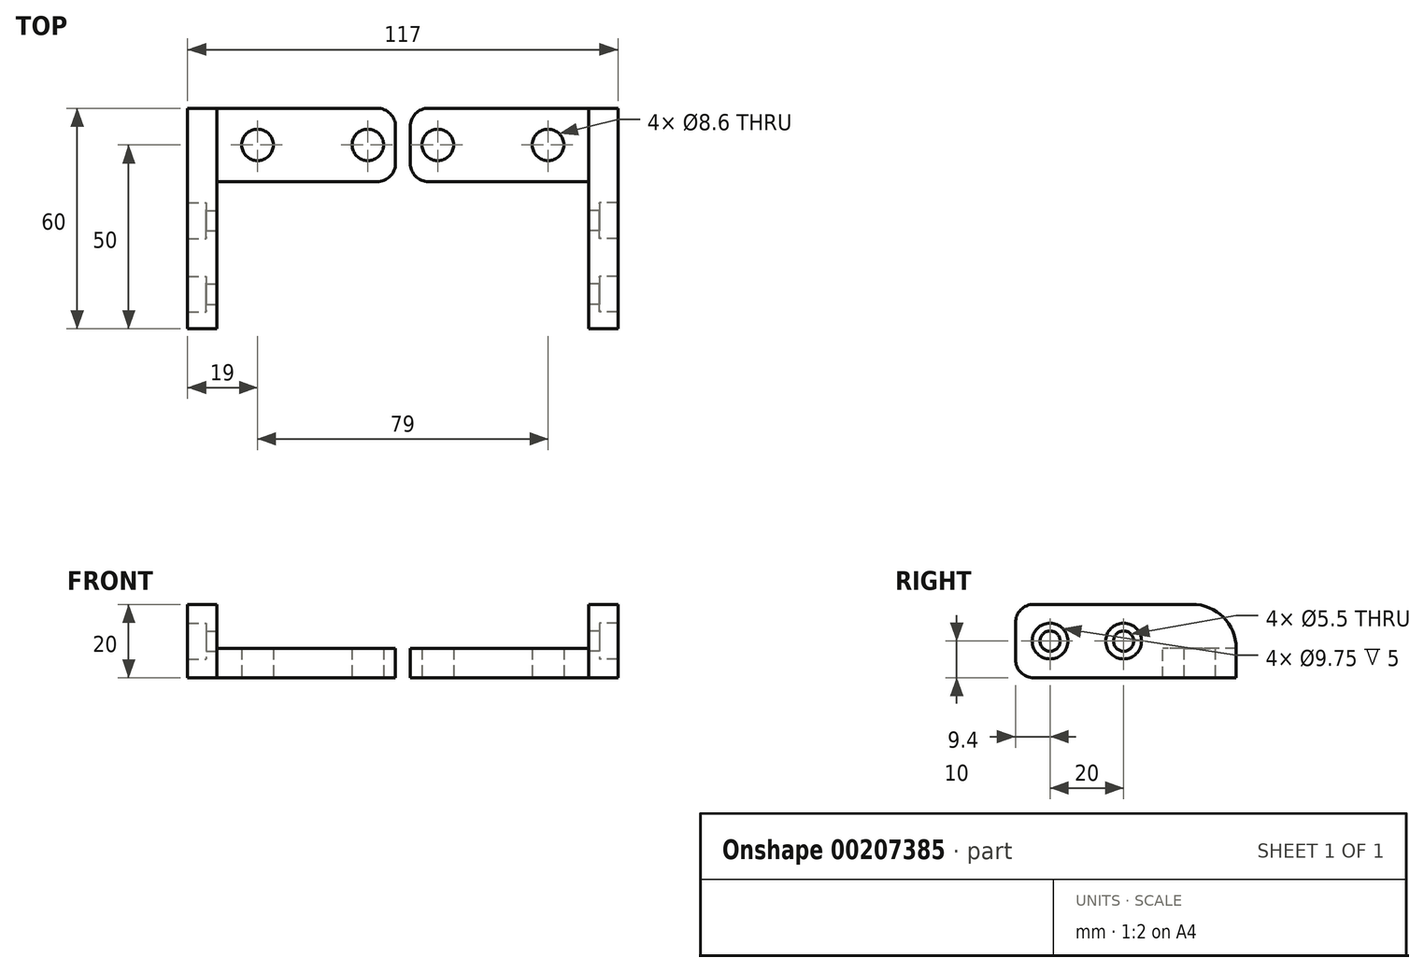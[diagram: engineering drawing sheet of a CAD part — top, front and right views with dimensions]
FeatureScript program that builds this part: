
annotation { "Feature Type Name" : "Feature", "Feature Type Description" : "" }
export const myFeature = defineFeature(function(context is Context, id is Id, definition is map)
    precondition{}
    {
        {
            var Q0;
            Q0=qCreatedBy(makeId("Top.planeOp"),FACE);
            var sketch = newSketch(context, id + "F0", { "sketchPlane" : qUnion([Q0])});
            skPoint(sketch, "E0", {"position": v(39.5, 50) * mm});
            skLineSegment(sketch, "E1.right", {"start": v(50.5, 60) * mm, "end": v(50.5, 40) * mm});
            skLineSegment(sketch, "E2", {"start": v(9.5, 29.4) * mm, "end": v(9.5, 9.4) * mm, "construction": true});
            skPoint(sketch, "E3", {"position": v(9.5, 19.4) * mm});
            skLineSegment(sketch, "E4.top", {"start": v(2, 0) * mm, "end": v(17, 0) * mm});
            skLineSegment(sketch, "E4.left", {"start": v(2, 60) * mm, "end": v(2, 0) * mm});
            skLineSegment(sketch, "E4.right", {"start": v(17, 40) * mm, "end": v(17, 0) * mm});
            skPoint(sketch, "E5", {"position": v(17, 19.4) * mm});
            skPoint(sketch, "E6", {"position": v(9.5, 0) * mm});
            skPoint(sketch, "E7", {"position": v(9.5, 29.4) * mm});
            skPoint(sketch, "E8", {"position": v(9.5, 9.4) * mm});
            skLineSegment(sketch, "E9", {"start": v(50.5, 40) * mm, "end": v(17, 40) * mm});
            skLineSegment(sketch, "E10", {"start": v(50.5, 60) * mm, "end": v(2, 60) * mm});
            skPoint(sketch, "E11", {"position": v(9.5, 50) * mm});
            skPoint(sketch, "E12", {"position": v(50.5, 50) * mm});
            skLineSegment(sketch, "E13", {"start": v(17, 40) * mm, "end": v(2, 40) * mm});
            skSolve(sketch);
        }
        {
            var Q0;
            Q0=makeQuery(id+"F0.imprint","IMPRINT",FACE,{"disambiguationData":[TD([[makeQuery(id+"F0.imprint","IMPRINT",EDGE,{"derivedFrom":sQuery(id+"F0.wireOp",EDGE,"E1.right")}),-1.0]])]});
            extrude(context, id + "F1", {"entities" : qUnion([Q0]), "oppositeDirection" : true, "depth" : 8 * mm, "offsetDistance" : 25 * mm});
        }
        {
            var Q0;
            Q0=sQuery(id+"F0.wireOp",VERTEX,"E11");
            var Q1;
            Q1=sQuery(id+"F0.wireOp",VERTEX,"E0");
            var Q2;
            Q2=makeQuery(id+"F1.opExtrude","SWEPT_BODY",BODY,{"disambiguationData":[OSD([sQuery(id+"F0.wireOp",EDGE,"E1.right"),sQuery(id+"F0.wireOp",EDGE,"E4.top"),sQuery(id+"F0.wireOp",EDGE,"E4.left"),sQuery(id+"F0.wireOp",EDGE,"E4.right"),sQuery(id+"F0.wireOp",EDGE,"E9"),sQuery(id+"F0.wireOp",EDGE,"E10")])]});
            hole(context, id + "F2", {"style" : HoleStyle.SIMPLE, "endStyle" : HoleEndStyle.THROUGH, "holeDiameter" : 8.6 * mm, "majorDiameter" : 5 * mm, "isTappedThrough" : true, "tappedDepth" : 12 * mm, "tapClearance" : 3, "locations" : qUnion([Q0, Q1]), "scope" : qUnion([Q2]), "startStyle" : HoleStartStyle.SKETCH});
        }
        {
            var Q0;
            Q0=makeQuery(id+"F1.opExtrude","SWEPT_FACE",FACE,{"disambiguationData":[OSD([sQuery(id+"F0.wireOp",EDGE,"E10")])]});
            var sketch = newSketch(context, id + "F3", { "sketchPlane" : qUnion([Q0])});
            skLineSegment(sketch, "E14.bottom", {"start": v(-50.5, -8) * mm, "end": v(-58.5, -8) * mm});
            skLineSegment(sketch, "E14.top", {"start": v(-50.5, 12) * mm, "end": v(-58.5, 12) * mm});
            skLineSegment(sketch, "E14.left", {"start": v(-50.5, -8) * mm, "end": v(-50.5, 12) * mm});
            skLineSegment(sketch, "E14.right", {"start": v(-58.5, -8) * mm, "end": v(-58.5, 12) * mm});
            skSolve(sketch);
        }
        {
            var Q0;
            {var subQ3=sQuery(id+"F3.wireOp",EDGE,"E14.bottom");Q0=makeQuery(id+"F3.imprint","IMPRINT",FACE,{"disambiguationData":[TD([[makeQuery(id+"F3.imprint","IMPRINT",EDGE,{"derivedFrom":subQ3}),-1.0]])]});}
            extrude(context, id + "F4", {"entities" : qUnion([Q0]), "operationType" : NewBodyOperationType.ADD, "oppositeDirection" : true, "depth" : 60 * mm, "offsetDistance" : 25 * mm});
        }
        {
            var Q0;
            Q0=makeQuery(id+"F4.opExtrude","SWEPT_FACE",FACE,{"disambiguationData":[OSD([sQuery(id+"F3.wireOp",EDGE,"E14.right")])]});
            var sketch = newSketch(context, id + "F5", { "sketchPlane" : qUnion([Q0])});
            skPoint(sketch, "E15", {"position": v(29.4, 2) * mm});
            skPoint(sketch, "E15.positionSnap0", {"position": v(60, 2) * mm});
            skPoint(sketch, "E16", {"position": v(9.4, 2) * mm});
            skPoint(sketch, "E17.0", {"position": v(50, 0) * mm});
            skSolve(sketch);
        }
        {
            var Q0;
            Q0=sQuery(id+"F5.wireOp",VERTEX,"E16");
            var Q1;
            Q1=sQuery(id+"F5.wireOp",VERTEX,"E15");
            var Q2;
            Q2=makeQuery(id+"F1.opExtrude","SWEPT_BODY",BODY,{"disambiguationData":[OSD([sQuery(id+"F0.wireOp",EDGE,"E1.right"),sQuery(id+"F0.wireOp",EDGE,"E4.top"),sQuery(id+"F0.wireOp",EDGE,"E4.left"),sQuery(id+"F0.wireOp",EDGE,"E4.right"),sQuery(id+"F0.wireOp",EDGE,"E9"),sQuery(id+"F0.wireOp",EDGE,"E10")])]});
            hole(context, id + "F6", {"style" : HoleStyle.C_BORE, "endStyle" : HoleEndStyle.BLIND, "standardTappedOrClearance" : lookupTablePath({ "fit" : "Normal", "standard" : "ISO", "size" : "M5", "type" : "Clearance" }), "standardBlindInLast" : lookupTablePath({ "fit" : "Normal", "standard" : "ISO", "engagement" : "75%", "pitch" : "0.8 mm", "size" : "M5", "type" : "Clearance & tapped" }), "holeDiameter" : 5.5 * mm, "cBoreDiameter" : 9.75 * mm, "cBoreDepth" : 5 * mm, "majorDiameter" : 5 * mm, "holeDepth" : 30 * mm, "isTappedThrough" : true, "tappedDepth" : 12 * mm, "tapClearance" : 3, "locations" : qUnion([Q0, Q1]), "scope" : qUnion([Q2]), "startStyle" : HoleStartStyle.SKETCH});
        }
        {
            var Q0;
            Q0=makeQuery(id+"F4.opExtrude","CAP_EDGE",EDGE,{"disambiguationData":[OSD([sQuery(id+"F3.wireOp",EDGE,"E14.top")])],"isStart":true});
            fillet(context, id + "F7", {"entities" : qUnion([Q0]), "radius" : 12 * mm, "tangentPropagation" : true, "allowEdgeOverflow" : false});
        }
        {
            var Q0;
            Q0=makeQuery(id+"F4.opExtrude","CAP_EDGE",EDGE,{"disambiguationData":[OSD([sQuery(id+"F3.wireOp",EDGE,"E14.top")])],"isStart":false});
            var Q1;
            Q1=makeQuery(id+"F4.opExtrude","CAP_EDGE",EDGE,{"disambiguationData":[OSD([sQuery(id+"F3.wireOp",EDGE,"E14.bottom")])],"isStart":false});
            var Q2;
            Q2=makeQuery(id+"F1.opExtrude","SWEPT_EDGE",EDGE,{"disambiguationData":[OSD([sQuery(id+"F0.wireOp",EDGE,"E4.left"),sQuery(id+"F0.wireOp",EDGE,"E13")])]});
            var Q3;
            Q3=makeQuery(id+"F1.opExtrude","SWEPT_EDGE",EDGE,{"disambiguationData":[OSD([sQuery(id+"F0.wireOp",EDGE,"E4.left"),sQuery(id+"F0.wireOp",EDGE,"E10")])]});
            var Q4;
            Q4=makeQuery(id+"F1.opExtrude","CAP_EDGE",EDGE,{"disambiguationData":[OSD([sQuery(id+"F0.wireOp",EDGE,"E1.right")])],"isStart":true});
            fillet(context, id + "F8", {"entities" : qUnion([Q0, Q1, Q2, Q3, Q4]), "radius" : 5 * mm, "tangentPropagation" : true, "allowEdgeOverflow" : false});
        }
        {
            var Q0;
            Q0=makeQuery(id+"F1.opExtrude","SWEPT_BODY",BODY,{"disambiguationData":[OSD([sQuery(id+"F0.wireOp",EDGE,"E1.right"),sQuery(id+"F0.wireOp",EDGE,"E4.left"),sQuery(id+"F0.wireOp",EDGE,"E9"),sQuery(id+"F0.wireOp",EDGE,"E10"),sQuery(id+"F0.wireOp",EDGE,"E13")])]});
            var Q1;
            Q1=qCreatedBy(makeId("Right.planeOp"),FACE);
            mirror(context, id + "F9", {"entities" : qUnion([Q0]), "mirrorPlane" : qUnion([Q1])});
        }
    });
